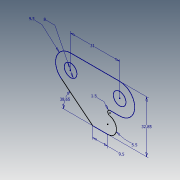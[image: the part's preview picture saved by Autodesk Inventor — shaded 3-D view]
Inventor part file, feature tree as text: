
AUTODESK INVENTOR PART (.ipt)
format: ipt  version: 2011 (Build 150229000, 229)  size: 76,800 bytes
history: native  units: mm (DEFAULTED — no unit token found)
features: sketch x1
ambient origin geometry x8: Origin, YZ Plane, XZ Plane, XY Plane, X Axis, Y Axis, Z Axis, Center Point
feature tree (1):
  sketch  "Sketch1"  dims[d0=9.5mm d1=8.0mm d2=31.0mm d3=1.5mm d4=5.5mm d6=9.5mm d7=6.745698mm d9=32.85mm]
